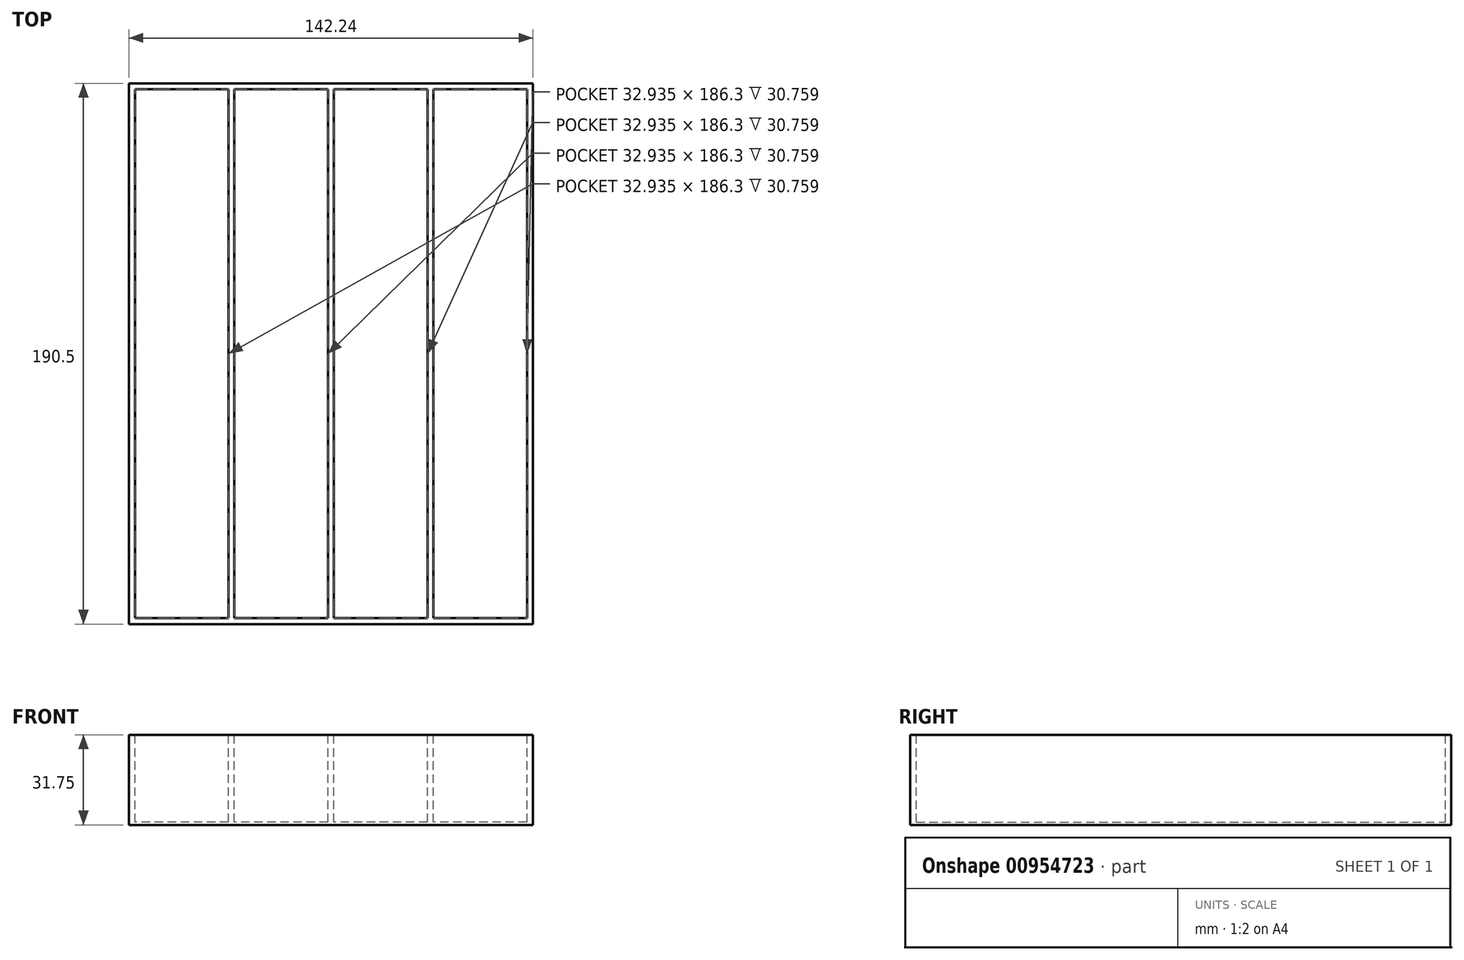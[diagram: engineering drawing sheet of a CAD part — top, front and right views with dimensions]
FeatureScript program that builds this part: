
annotation { "Feature Type Name" : "Feature", "Feature Type Description" : "" }
export const myFeature = defineFeature(function(context is Context, id is Id, definition is map)
    precondition{}
    {
        {
            var Q0;
            Q0=qCreatedBy(makeId("Top.planeOp"),FACE);
            var sketch = newSketch(context, id + "F0", { "sketchPlane" : qUnion([Q0])});
            skLineSegment(sketch, "E0.bottom", {"start": v(0, 0) * mm, "end": v(142.24, 0) * mm});
            skLineSegment(sketch, "E0.top", {"start": v(0, 190.5) * mm, "end": v(142.24, 190.5) * mm});
            skLineSegment(sketch, "E0.left", {"start": v(0, 0) * mm, "end": v(0, 190.5) * mm});
            skLineSegment(sketch, "E0.right", {"start": v(142.24, 0) * mm, "end": v(142.24, 190.5) * mm});
            skSolve(sketch);
        }
        {
            var Q0;
            Q0=qSketchRegion(id+"F0",true);
            extrude(context, id + "F1", {"entities" : qUnion([Q0]), "depth" : 31.75 * mm, "offsetDistance" : 25 * mm});
        }
        {
            var Q0;
            Q0=makeQuery(id+"F1.opExtrude","CAP_FACE",FACE,{"disambiguationData":[OSD([sQuery(id+"F0.wireOp",EDGE,"E0.bottom"),sQuery(id+"F0.wireOp",EDGE,"E0.top"),sQuery(id+"F0.wireOp",EDGE,"E0.left"),sQuery(id+"F0.wireOp",EDGE,"E0.right")])],"isStart":false});
            var sketch = newSketch(context, id + "F2", { "sketchPlane" : qUnion([Q0])});
            skLineSegment(sketch, "E1.bottom", {"start": v(2.1, 188.4) * mm, "end": v(35.04, 188.4) * mm});
            skLineSegment(sketch, "E1.top", {"start": v(2.1, 2.1) * mm, "end": v(35.04, 2.1) * mm});
            skLineSegment(sketch, "E1.left", {"start": v(2.1, 188.4) * mm, "end": v(2.1, 2.1) * mm});
            skLineSegment(sketch, "E1.right", {"start": v(35.04, 188.4) * mm, "end": v(35.04, 2.1) * mm});
            skLineSegment(sketch, "E2.bottom", {"start": v(37.14, 188.4) * mm, "end": v(70.07, 188.4) * mm});
            skLineSegment(sketch, "E2.top", {"start": v(37.14, 2.1) * mm, "end": v(70.07, 2.1) * mm});
            skLineSegment(sketch, "E2.left", {"start": v(37.14, 188.4) * mm, "end": v(37.14, 2.1) * mm});
            skLineSegment(sketch, "E2.right", {"start": v(70.07, 188.4) * mm, "end": v(70.07, 2.1) * mm});
            skLineSegment(sketch, "E3.bottom", {"start": v(72.17, 188.4) * mm, "end": v(105.1, 188.4) * mm});
            skLineSegment(sketch, "E3.top", {"start": v(72.17, 2.1) * mm, "end": v(105.1, 2.1) * mm});
            skLineSegment(sketch, "E3.left", {"start": v(72.17, 188.4) * mm, "end": v(72.17, 2.1) * mm});
            skLineSegment(sketch, "E3.right", {"start": v(105.1, 188.4) * mm, "end": v(105.1, 2.1) * mm});
            skLineSegment(sketch, "E4.bottom", {"start": v(107.2, 188.4) * mm, "end": v(140.14, 188.4) * mm});
            skLineSegment(sketch, "E4.top", {"start": v(107.2, 2.1) * mm, "end": v(140.14, 2.1) * mm});
            skLineSegment(sketch, "E4.left", {"start": v(107.2, 188.4) * mm, "end": v(107.2, 2.1) * mm});
            skLineSegment(sketch, "E4.right", {"start": v(140.14, 188.4) * mm, "end": v(140.14, 2.1) * mm});
            skSolve(sketch);
        }
        {
            var Q0;
            Q0 = qSketchRegion(id + "F2", true);
            var Q1;
            Q1=makeQuery(id+"F1.opExtrude","CAP_FACE",FACE,{"disambiguationData":[OSD([sQuery(id+"F0.wireOp",EDGE,"E0.bottom"),sQuery(id+"F0.wireOp",EDGE,"E0.top"),sQuery(id+"F0.wireOp",EDGE,"E0.left"),sQuery(id+"F0.wireOp",EDGE,"E0.right")])],"isStart":true});
            extrude(context, id + "F3", {"entities" : qUnion([Q0]), "operationType" : NewBodyOperationType.REMOVE, "endBound" : BoundingType.UP_TO_SURFACE, "oppositeDirection" : true, "depth" : 30.76 * mm, "endBoundEntityFace" : qUnion([Q1]), "hasOffset" : true, "offsetDistance" : 1 * mm});
        }
    });
